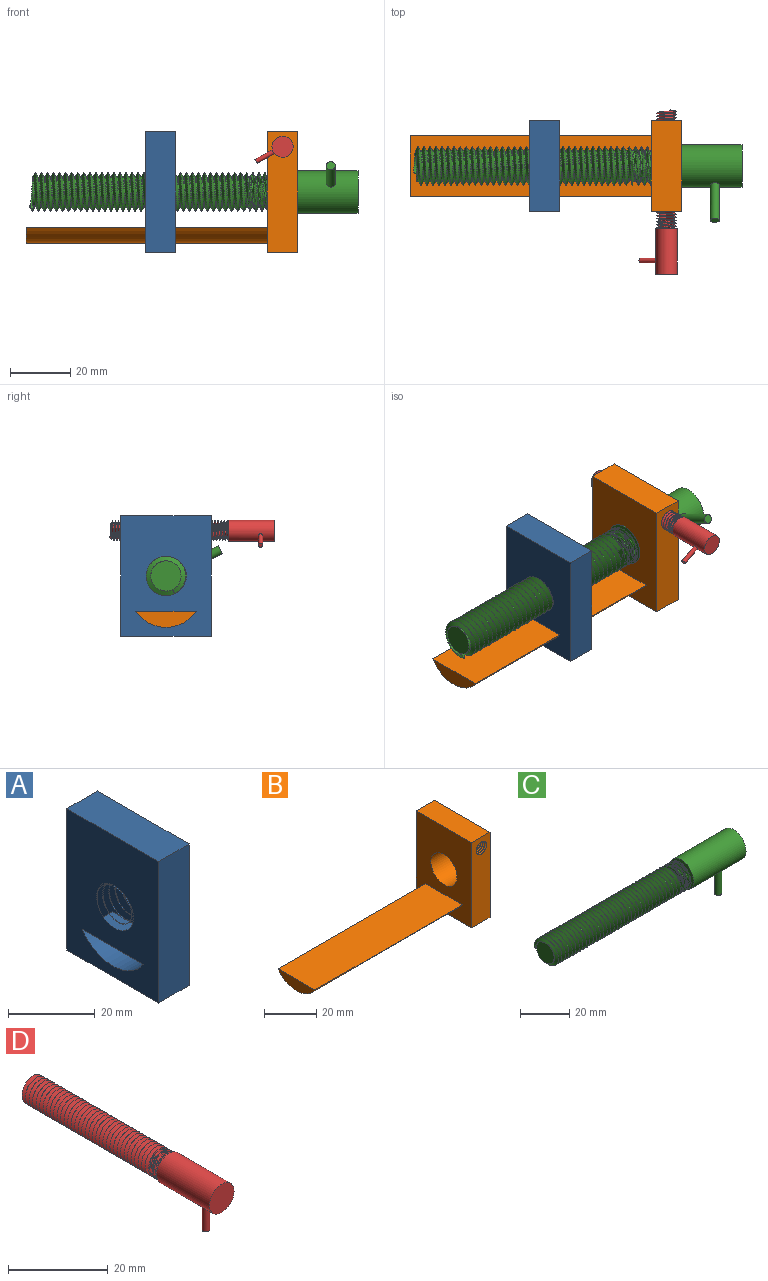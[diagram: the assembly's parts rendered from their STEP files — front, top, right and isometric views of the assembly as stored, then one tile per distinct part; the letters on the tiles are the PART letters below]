
ASSEMBLY  parts=4 mates=3
PART A: 9 faces, bbox 10x30x40 mm
  f0: plane 40x30mm, normal (-1,0,0), area 1010.7mm2, adj f2,f3,f4,f5,f6,f7,f8
  f1: plane 40x30mm, normal (1,0,0), area 1010.7mm2, adj f2,f3,f4,f5,f6,f7,f8
  f2: plane 40x10mm, normal (0,-1,0), area 400mm2, adj f0,f1,f4,f5
  f3: plane 40x10mm, normal (0,1,0), area 400mm2, adj f0,f1,f4,f5
  f4: plane 30x10mm, normal (0,0,1), area 300mm2, adj f0,f1,f2,f3
  f5: plane 30x10mm, normal (0,0,-1), area 300mm2, adj f0,f1,f2,f3
  f6: plane 20x10mm, normal (0,0,-1), area 200mm2, adj f0,f1,f7
  f7: cylinder r=12mm len=20mm, axis (1,0,0), area 236.4mm2, adj f0,f1,f6
  f8: cylinder r=5.2mm len=10.4mm, axis (1,0,0), area 25.7mm2, adj f0,f1
PART B: 13 faces, bbox 90.5x31.5x40.5 mm
  f0: plane 40.47x10.47mm, normal (0,-1,0), area 375.2mm2, adj f5,f6,f7,f8,f10,f11,f12
  f1: plane 40.47x10.47mm, normal (0,1,0), area 375.2mm2, adj f5,f6,f7,f8,f10,f11,f12
  f2: plane 80x20mm, normal (0,0,1), area 1600mm2, adj f3,f4,f5
  f3: cylinder r=12mm len=80mm, axis (1,0,0), area 1891.4mm2, adj f2,f4,f5
  f4: plane 20x5.37mm, normal (-1,0,0), area 75.5mm2, adj f2,f3
  f5: plane 40x30mm, normal (-1,0,0), area 966.1mm2, adj f0,f1,f2,f3,f6,f7,f9
  f6: plane 30x10mm, normal (0,0,1), area 300mm2, adj f0,f1,f5,f8
  f7: plane 30x10mm, normal (0,0,-1), area 300mm2, adj f0,f1,f5,f8
  f8: plane 40x30mm, normal (1,0,0), area 1041.6mm2, adj f0,f1,f6,f7,f9
  f9: cylinder r=7.1mm len=14.2mm, axis (-1,0,0), area 446.1mm2, adj f5,f8
  f10: cylinder r=2.5mm len=30mm, axis (0,-1,0), area 331.5mm2, adj f0,f1,f11,f12
  f11: bspline ~30.9x7.51mm, area 460.2mm2, adj f0,f1,f10,f12
  f12: bspline ~31.07x7.51mm, area 462.1mm2, adj f0,f1,f10,f11
PART C: 11 faces, bbox 109.7x14.9x28.4 mm
  f0: cylinder r=7mm len=30mm, axis (-1,0,0), area 1312.3mm2, adj f7,f8,f9
  f1: cylinder r=5mm len=78mm, axis (1,0,0), area -1517.9mm2, adj f2,f3,f4,f6,f7
  f2: bspline ~79.8x15.01mm, area 2398.9mm2, adj f1,f3,f5,f6,f7
  f3: bspline ~78.8x12.99mm, area 2391.8mm2, adj f1,f2,f6,f7
  f4: plane 10.07x10.07mm, normal (-1,0,0), area 78.6mm2, adj f1,f5
  f5: bspline ~9.07x5mm, area 5mm2, adj f2,f4,f6
  f6: plane 1.6x1.5mm, normal (-0.06,0,-1), area 1.2mm2, adj f1,f2,f3,f5
  f7: plane 14.93x14.93mm, normal (-1,0,0), area 54.6mm2, adj f0,f1,f2,f3
  f8: plane 14x14mm, normal (1,0,0), area 153.9mm2, adj f0
  f9: cylinder r=1.5mm len=13mm, axis (0,0,-1), area 122.5mm2, adj f0,f10
  f10: plane 3x3mm, normal (0,0,-1), area 7.1mm2, adj f9
PART D: 11 faces, bbox 7.5x54.9x14.2 mm
  f0: cylinder r=3.5mm len=15mm, axis (0,1,0), area 328.1mm2, adj f7,f8,f9
  f1: cylinder r=2.5mm len=39mm, axis (0,-1,0), area -401.7mm2, adj f2,f3,f4,f6,f7
  f2: bspline ~39.9x7.51mm, area 599.7mm2, adj f1,f3,f5,f6,f7
  f3: bspline ~39.57x7.51mm, area 598mm2, adj f1,f2,f6,f7
  f4: plane 5.03x5.03mm, normal (0,1,0), area 19.6mm2, adj f1,f5
  f5: bspline ~5.03x2.91mm, area 1.3mm2, adj f2,f4,f6
  f6: plane 0.8x0.75mm, normal (0,0.06,-1), area 0.3mm2, adj f1,f2,f3,f5
  f7: plane 7.47x7.47mm, normal (0,1,0), area 13.7mm2, adj f0,f1,f2,f3
  f8: plane 7x7mm, normal (0,-1,0), area 38.5mm2, adj f0
  f9: cylinder r=0.75mm len=6.5mm, axis (0,0,-1), area 30.6mm2, adj f0,f10
  f10: plane 1.5x1.5mm, normal (0,0,-1), area 1.8mm2, adj f9
PLACE A t=(34.64,0,0)mm
PLACE B at identity fixed
PLACE C rot(axis=(-1,0,0),115.8deg) t=(2,-18.01,28.7)mm
PLACE D rot(axis=(0,1,0),61.3deg) t=(-9.92,0.17,53.25)mm
MATE revolute C.f0 <-> B.f9  axis (-1,0,0) through (35,0,20)mm
MATE cylindrical B.f10 <-> D.f0  axis (0,-1,0) through (40,-36,35)mm
MATE slider A.f0 <-> B.f4  axis (-1,0,0) through (-5.36,0,8.37)mm
